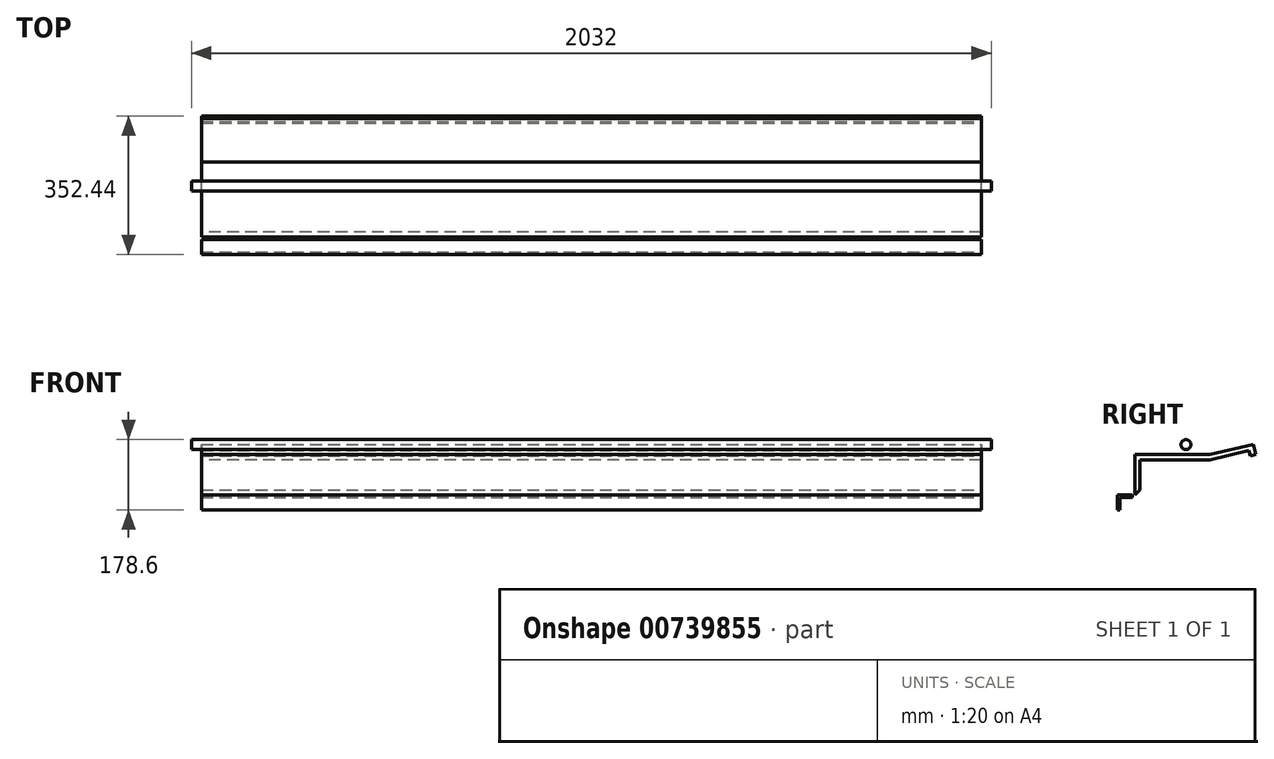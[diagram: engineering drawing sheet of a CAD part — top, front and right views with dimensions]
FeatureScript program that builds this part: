
annotation { "Feature Type Name" : "Feature", "Feature Type Description" : "" }
export const myFeature = defineFeature(function(context is Context, id is Id, definition is map)
    precondition{}
    {
        {
            var Q0;
            Q0=qCreatedBy(makeId("Right.planeOp"),FACE);
            var sketch = newSketch(context, id + "F0", { "sketchPlane" : qUnion([Q0])});
            skLineSegment(sketch, "E0", {"start": v(0, 0) * mm, "end": v(0, 101.6) * mm});
            skLineSegment(sketch, "E1", {"start": v(0, 101.6) * mm, "end": v(12.7, 101.6) * mm});
            skLineSegment(sketch, "E2", {"start": v(12.7, 101.6) * mm, "end": v(12.7, 12.7) * mm});
            skLineSegment(sketch, "E3", {"start": v(12.7, 12.7) * mm, "end": v(0, 0) * mm});
            skLineSegment(sketch, "E4", {"start": v(0, 0) * mm, "end": v(-6.35, 0) * mm});
            skLineSegment(sketch, "E5", {"start": v(-6.35, 0) * mm, "end": v(-44.45, 0) * mm});
            skLineSegment(sketch, "E6", {"start": v(-44.45, 0) * mm, "end": v(-44.45, -38.1) * mm});
            skLineSegment(sketch, "E7", {"start": v(-44.45, -38.1) * mm, "end": v(-38.1, -38.1) * mm});
            skLineSegment(sketch, "E8", {"start": v(-38.1, -38.1) * mm, "end": v(-38.1, -6.35) * mm});
            skLineSegment(sketch, "E9", {"start": v(-38.1, -6.35) * mm, "end": v(-6.35, -6.35) * mm});
            skLineSegment(sketch, "E10", {"start": v(-6.35, -6.35) * mm, "end": v(-6.35, 0) * mm});
            skSolve(sketch);
        }
        {
            var Q0;
            Q0=makeQuery(id+"F0.imprint","IMPRINT",FACE,{"disambiguationData":[TD([[makeQuery(id+"F0.imprint","IMPRINT",EDGE,{"derivedFrom":sQuery(id+"F0.wireOp",EDGE,"E0")}),-1.0]])]});
            var Q1;
            Q1=makeQuery(id+"F0.imprint","IMPRINT",FACE,{"disambiguationData":[TD([[makeQuery(id+"F0.imprint","IMPRINT",EDGE,{"derivedFrom":sQuery(id+"F0.wireOp",EDGE,"E5")}),1.0]])]});
            extrude(context, id + "F1", {"entities" : qUnion([Q0, Q1]), "oppositeDirection" : true, "depth" : 1981.2 * mm, "offsetDistance" : 25.4 * mm});
        }
        {
            var Q0;
            Q0=qCreatedBy(makeId("Right.planeOp"),FACE);
            var sketch = newSketch(context, id + "F2", { "sketchPlane" : qUnion([Q0])});
            skLineSegment(sketch, "E11", {"start": v(0, 102.4) * mm, "end": v(190.5, 102.4) * mm});
            skLineSegment(sketch, "E12", {"start": v(190.5, 102.4) * mm, "end": v(301.7, 128.85) * mm});
            skLineSegment(sketch, "E13", {"start": v(301.7, 128.85) * mm, "end": v(304.64, 116.5) * mm});
            skLineSegment(sketch, "E14", {"start": v(304.64, 116.5) * mm, "end": v(190.5, 89.34) * mm});
            skLineSegment(sketch, "E15", {"start": v(190.5, 89.34) * mm, "end": v(0, 89.34) * mm});
            skLineSegment(sketch, "E16", {"start": v(0, 89.34) * mm, "end": v(0, 102.4) * mm});
            skLineSegment(sketch, "E17", {"start": v(304.64, 116.5) * mm, "end": v(307.99, 102.4) * mm});
            skLineSegment(sketch, "E18", {"start": v(307.99, 102.4) * mm, "end": v(293.63, 98.98) * mm});
            skLineSegment(sketch, "E19", {"start": v(293.63, 98.98) * mm, "end": v(290.27, 113.08) * mm});
            skSolve(sketch);
        }
        {
            var Q0;
            Q0 = qSketchRegion(id + "F2", true);
            extrude(context, id + "F3", {"entities" : qUnion([Q0]), "operationType" : NewBodyOperationType.ADD, "oppositeDirection" : true, "depth" : 1981.2 * mm, "offsetDistance" : 25.4 * mm});
        }
        {
            var Q0;
            Q0=makeQuery(id+"F3.boolean.opBoolean","MERGE",FACE,{"derivedFrom":[makeQuery(id+"F1.opExtrude","CAP_FACE",FACE,{"disambiguationData":[OSD([sQuery(id+"F0.wireOp",EDGE,"E0"),sQuery(id+"F0.wireOp",EDGE,"E1"),sQuery(id+"F0.wireOp",EDGE,"E2"),sQuery(id+"F0.wireOp",EDGE,"E3")])],"isStart":true}),makeQuery(id+"F3.opExtrude","CAP_FACE",FACE,{"disambiguationData":[OSD([sQuery(id+"F2.wireOp",EDGE,"E11"),sQuery(id+"F2.wireOp",EDGE,"E12"),sQuery(id+"F2.wireOp",EDGE,"E13"),sQuery(id+"F2.wireOp",EDGE,"E14"),sQuery(id+"F2.wireOp",EDGE,"E15"),sQuery(id+"F2.wireOp",EDGE,"E16"),sQuery(id+"F2.wireOp",EDGE,"E17"),sQuery(id+"F2.wireOp",EDGE,"E18"),sQuery(id+"F2.wireOp",EDGE,"E19")])],"isStart":true})]});
            var sketch = newSketch(context, id + "F4", { "sketchPlane" : qUnion([Q0])});
            skLineSegment(sketch, "E20", {"start": v(130.1, 102.4) * mm, "end": v(130.1, 127.8) * mm});
            skCircle(sketch, "E21", {"center": v(130.1, 127.8) * mm, "radius": 12.7 * mm});
            skSolve(sketch);
        }
        {
            var Q0;
            Q0=makeQuery(id+"F4.imprint","IMPRINT",FACE,{"disambiguationData":[TD([[makeQuery(id+"F4.imprint","IMPRINT",EDGE,{"derivedFrom":sQuery(id+"F4.wireOp",EDGE,"E21")}),1.0]])]});
            extrude(context, id + "F5", {"entities" : qUnion([Q0]), "depth" : 25.4 * mm, "offsetDistance" : 25.4 * mm, "hasSecondDirection" : true, "secondDirectionOppositeDirection" : true, "secondDirectionDepth" : 2006.6 * mm});
        }
    });
